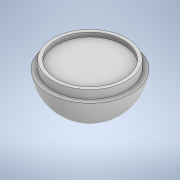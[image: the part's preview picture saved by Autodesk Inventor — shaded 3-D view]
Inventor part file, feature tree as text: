
AUTODESK INVENTOR PART (.ipt)
format: ipt  version: 2022 (Build 260153000, 153)  size: 146,944 bytes
history: native  units: in
note: dims shown in document units (in); Inventor stores cm internally (conversion verified against a paired STEP export)
features: sketch x5, extrude x4, revolve x1
ambient origin geometry x8: Origin, YZ Plane, XZ Plane, XY Plane, X Axis, Y Axis, Z Axis, Center Point
bodies: Solid1 (feature_tree)
feature tree (10):
  revolve  "Revolution1"  Angle=180.0deg
  extrude  "Extrusion1"  Depth=1.1in
  extrude  "Extrusion2"  Depth=0.125in TaperAngle=0.0deg
  extrude  "Extrusion3"  Depth=0.125in
  extrude  "Extrusion4"  Depth=0.125in
  sketch  "Sketch1"  dims[d0=1.25in d1=180.0deg]
  sketch  "Sketch2"  dims[d2=180.0deg d3=1.1in]
  sketch  "Sketch3"  dims[d4=1.0in d5=0.125in d6=0.0in]
  sketch  "Sketch4"  dims[d7=0.125in d8=0.0in d9=2.5in]
  sketch  "Sketch5"  dims[d10=2.0in d11=1.2in d12=0.0in d13=0.0in d14=0.125in d15=0.25in d16=0.0in]
